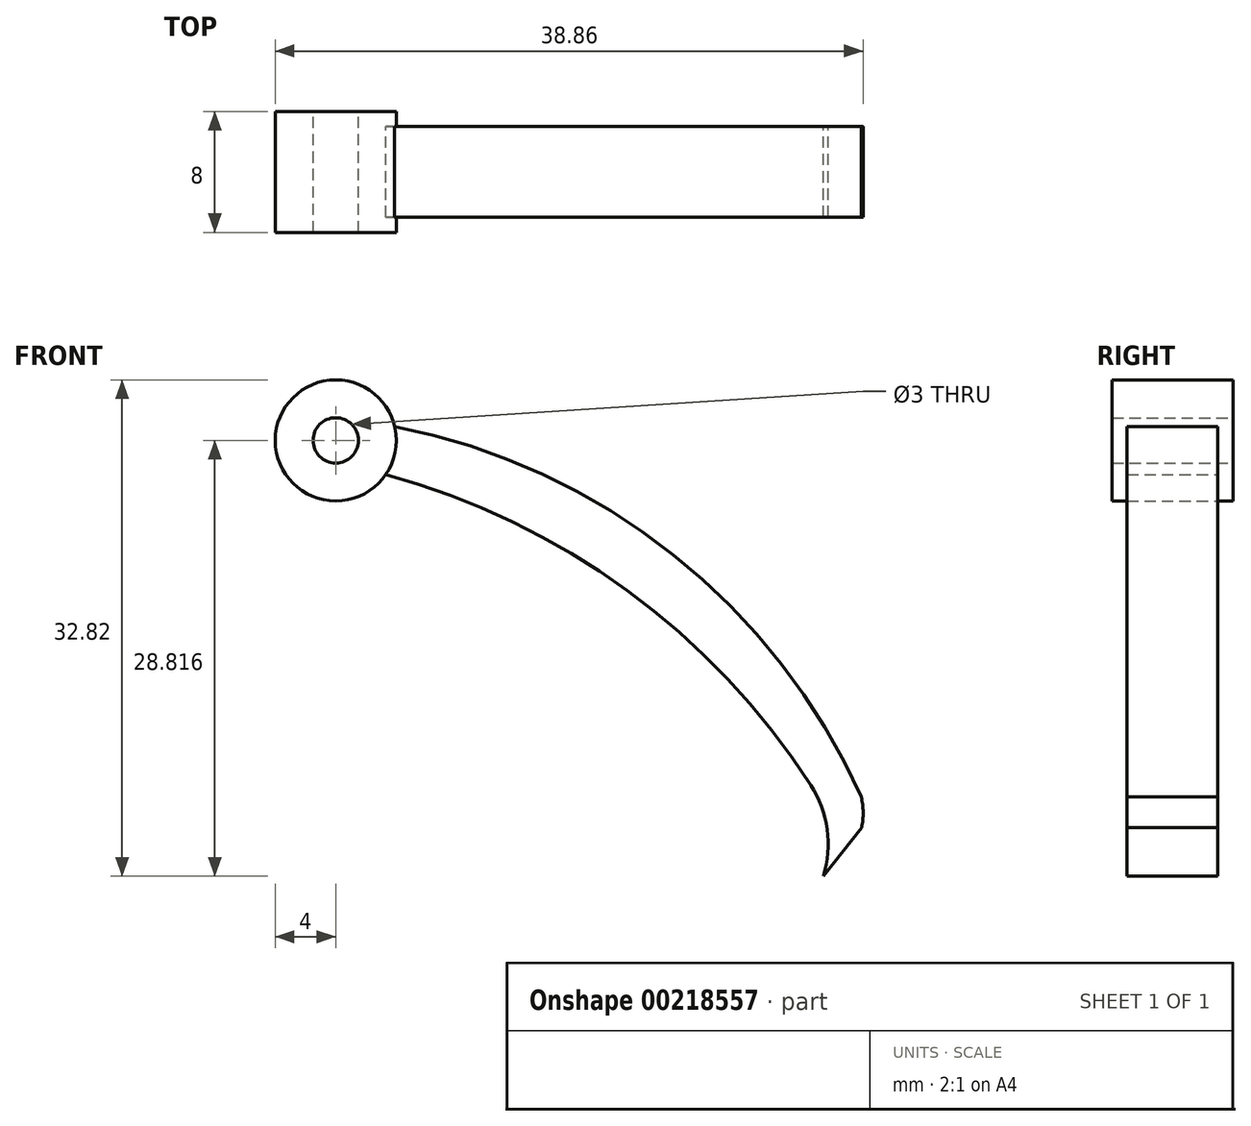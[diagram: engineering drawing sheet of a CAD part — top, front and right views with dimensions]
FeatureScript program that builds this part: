
annotation { "Feature Type Name" : "Feature", "Feature Type Description" : "" }
export const myFeature = defineFeature(function(context is Context, id is Id, definition is map)
    precondition{}
    {
        {
            var Q0;
            Q0=qCreatedBy(makeId("Front.planeOp"),FACE);
            var sketch = newSketch(context, id + "F0", { "sketchPlane" : qUnion([Q0])});
            skPoint(sketch, "E0.center", {"position": v(-0.03, 0) * mm});
            skLineSegment(sketch, "E1", {"start": v(0, 0) * mm, "end": v(-0.03, 0) * mm});
            skLineSegment(sketch, "E2", {"start": v(-0.03, 0) * mm, "end": v(0, 0.04) * mm});
            skArc(sketch, "E3", {"start": v(31.4, 46.86) * mm, "mid": v(19.25, 59.73) * mm, "end": v(3.3, 67.38) * mm});
            skPoint(sketch, "E3.startSnap0", {"position": v(33.76, 42.76) * mm});
            skLineSegment(sketch, "E4", {"start": v(32.2, 40.8) * mm, "end": v(32.2, 40.82) * mm});
            skLineSegment(sketch, "E5.trimOffspring", {"start": v(32.2, 40.8) * mm, "end": v(34.76, 44.04) * mm});
            skPoint(sketch, "E6.orphan", {"position": v(33.76, 42.78) * mm});
            skArc(sketch, "E7", {"start": v(32.2, 40.8) * mm, "mid": v(32.49, 43.92) * mm, "end": v(31.4, 46.86) * mm});
            skArc(sketch, "E8", {"start": v(34.76, 44.04) * mm, "mid": v(34.86, 45.06) * mm, "end": v(34.73, 46.08) * mm});
            skArc(sketch, "E9.trimOffspring", {"start": v(34.73, 46.08) * mm, "mid": v(22.3, 62.1) * mm, "end": v(3.9, 70.57) * mm});
            skCircle(sketch, "E10", {"center": v(0, 69.65) * mm, "radius": 4 * mm});
            skCircle(sketch, "E11", {"center": v(0, 69.65) * mm, "radius": 1.5 * mm});
            skSolve(sketch);
        }
        {
            var Q0;
            {var subQ2=sQuery(id+"F0.wireOp",EDGE,"E3");Q0=makeQuery(id+"F0.imprint","IMPRINT",FACE,{"disambiguationData":[TD([[makeQuery(id+"F0.imprint","IMPRINT",EDGE,{"derivedFrom":subQ2}),-1.0]])]});}
            extrude(context, id + "F1", {"entities" : qUnion([Q0]), "depth" : 6 * mm, "symmetric" : true});
        }
        {
            var Q0;
            Q0=makeQuery(id+"F0.imprint","IMPRINT",FACE,{"disambiguationData":[TD([[makeQuery(id+"F0.imprint","IMPRINT",EDGE,{"derivedFrom":sQuery(id+"F0.wireOp",EDGE,"E11")}),-1.0]])]});
            extrude(context, id + "F2", {"entities" : qUnion([Q0]), "operationType" : NewBodyOperationType.ADD, "depth" : 8 * mm, "symmetric" : true});
        }
    });
